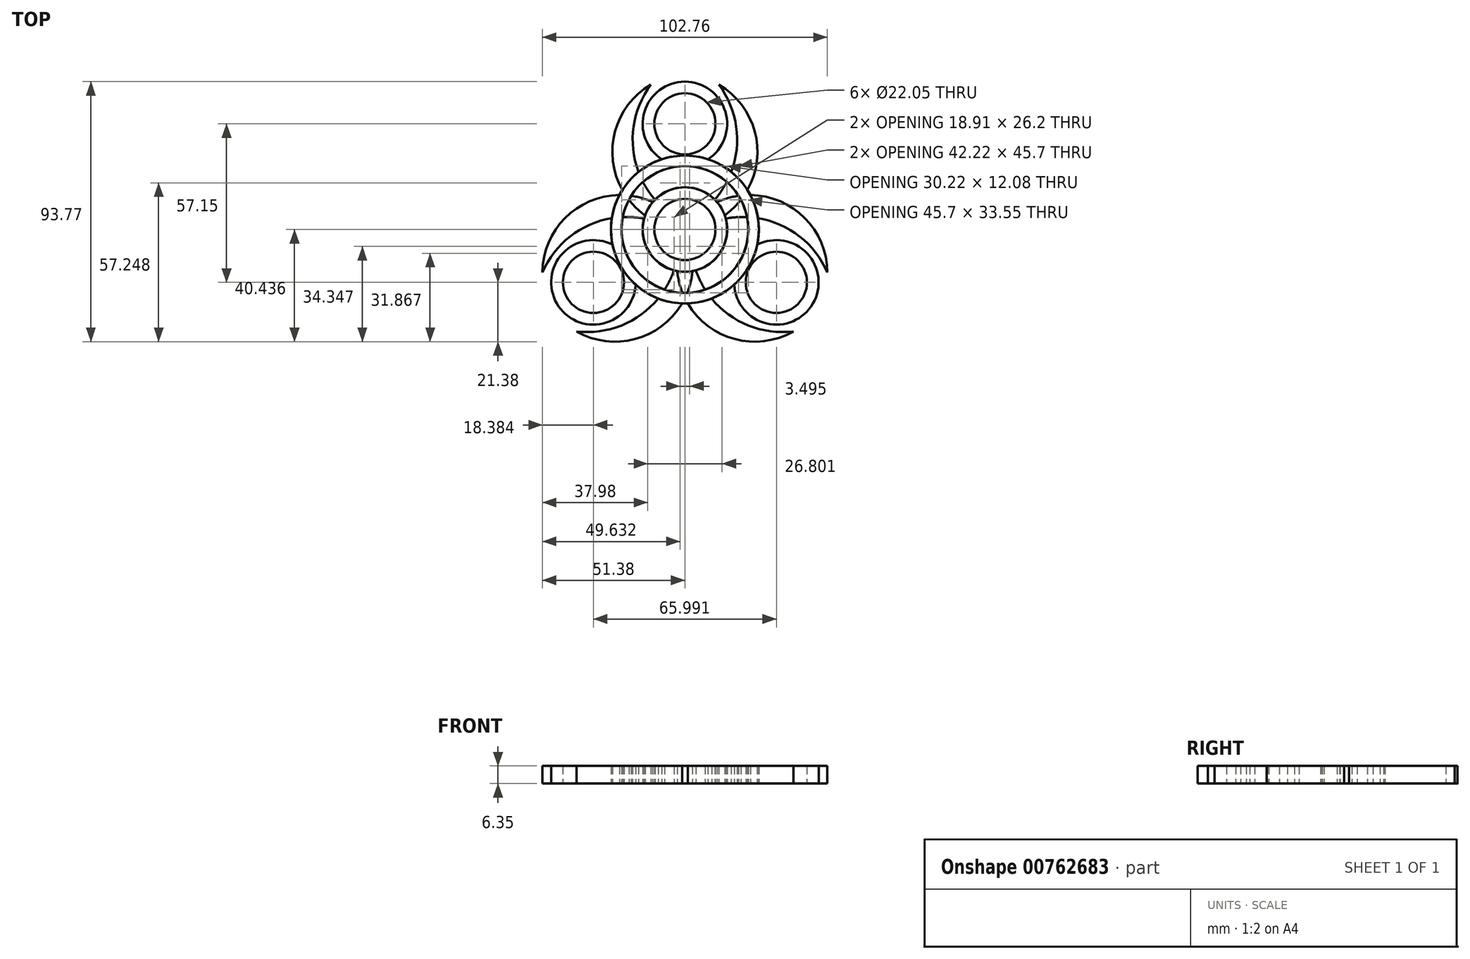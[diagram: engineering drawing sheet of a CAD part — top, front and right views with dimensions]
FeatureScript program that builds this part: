
annotation { "Feature Type Name" : "Feature", "Feature Type Description" : "" }
export const myFeature = defineFeature(function(context is Context, id is Id, definition is map)
    precondition{}
    {
        {
            var Q0;
            Q0=qCreatedBy(makeId("Top.planeOp"),FACE);
            var sketch = newSketch(context, id + "F0", { "sketchPlane" : qUnion([Q0])});
            skCircle(sketch, "E0", {"center": v(0, 0) * mm, "radius": 15.24 * mm});
            skCircle(sketch, "E1", {"center": v(0, 0) * mm, "radius": 11.02 * mm});
            skCircle(sketch, "E2", {"center": v(0, 0) * mm, "radius": 26.67 * mm});
            skCircle(sketch, "E3", {"center": v(0, 0) * mm, "radius": 22.86 * mm});
            skCircle(sketch, "E4", {"center": v(0, 38.1) * mm, "radius": 15.24 * mm});
            skCircle(sketch, "E5", {"center": v(0, 38.1) * mm, "radius": 11.02 * mm});
            skArc(sketch, "E6", {"start": v(-12.25, 52.25) * mm, "mid": v(-18.83, 31.26) * mm, "end": v(-10.78, 10.78) * mm});
            skArc(sketch, "E7", {"start": v(-12.25, 52.25) * mm, "mid": v(-26.15, 29.26) * mm, "end": v(-14.36, 5.12) * mm});
            skArc(sketch, "E8.MirrorCS", {"start": v(12.25, 52.25) * mm, "mid": v(18.83, 31.26) * mm, "end": v(10.78, 10.78) * mm});
            skArc(sketch, "E9.MirrorCS", {"start": v(12.25, 52.25) * mm, "mid": v(26.15, 29.26) * mm, "end": v(14.36, 5.12) * mm});
            skSolve(sketch);
        }
        {
            var Q0;
            {var subQ0=sQuery(id+"F0.wireOp",EDGE,"E6");var subQ1=sQuery(id+"F0.wireOp",EDGE,"E2");var subQ2=makeQuery(id+"F0.imprint","INTERSECT",VERTEX,{"derivedFrom":[subQ1,subQ0]});Q0=makeQuery(id+"F0.imprint","IMPRINT",FACE,{"disambiguationData":[TD([[makeQuery(id+"F0.imprint","IMPRINT",EDGE,{"disambiguationData":[TD([[subQ2,-1.0]])],"derivedFrom":subQ1}),-1.0]])]});}
            var Q1;
            Q1=makeQuery(id+"F0.imprint","IMPRINT",FACE,{"disambiguationData":[TD([[makeQuery(id+"F0.imprint","IMPRINT",EDGE,{"derivedFrom":sQuery(id+"F0.wireOp",EDGE,"E5")}),-1.0]])]});
            var Q2;
            {var subQ0=sQuery(id+"F0.wireOp",EDGE,"E4");var subQ1=sQuery(id+"F0.wireOp",EDGE,"E2");var subQ2=makeQuery(id+"F0.imprint","INTERSECT",VERTEX,{"disambiguationData":[OD(0.0)],"derivedFrom":[subQ1,subQ0]});Q2=makeQuery(id+"F0.imprint","IMPRINT",FACE,{"disambiguationData":[TD([[makeQuery(id+"F0.imprint","IMPRINT",EDGE,{"disambiguationData":[TD([[subQ2,-1.0]])],"derivedFrom":subQ1}),1.0]])]});}
            var Q3;
            {var subQ0=sQuery(id+"F0.wireOp",EDGE,"E4");var subQ1=sQuery(id+"F0.wireOp",EDGE,"E2");var subQ2=makeQuery(id+"F0.imprint","INTERSECT",VERTEX,{"disambiguationData":[OD(1.0)],"derivedFrom":[subQ1,subQ0]});Q3=makeQuery(id+"F0.imprint","IMPRINT",FACE,{"disambiguationData":[TD([[makeQuery(id+"F0.imprint","IMPRINT",EDGE,{"disambiguationData":[TD([[subQ2,-1.0]])],"derivedFrom":subQ1}),1.0]])]});}
            var Q4;
            {var subQ0=sQuery(id+"F0.wireOp",EDGE,"E6");var subQ1=sQuery(id+"F0.wireOp",EDGE,"E2");var subQ2=makeQuery(id+"F0.imprint","INTERSECT",VERTEX,{"derivedFrom":[subQ1,subQ0]});Q4=makeQuery(id+"F0.imprint","IMPRINT",FACE,{"disambiguationData":[TD([[makeQuery(id+"F0.imprint","IMPRINT",EDGE,{"disambiguationData":[TD([[subQ2,-1.0]])],"derivedFrom":subQ1}),1.0]])]});}
            var Q5;
            {var subQ0=sQuery(id+"F0.wireOp",EDGE,"E6");var subQ1=sQuery(id+"F0.wireOp",EDGE,"E0");var subQ2=makeQuery(id+"F0.imprint","INTERSECT",VERTEX,{"derivedFrom":[subQ1,subQ0]});Q5=makeQuery(id+"F0.imprint","IMPRINT",FACE,{"disambiguationData":[TD([[makeQuery(id+"F0.imprint","IMPRINT",EDGE,{"disambiguationData":[TD([[subQ2,-1.0]])],"derivedFrom":subQ1}),-1.0]])]});}
            var Q6;
            {var subQ0=sQuery(id+"F0.wireOp",EDGE,"E9.MirrorCS");var subQ1=sQuery(id+"F0.wireOp",EDGE,"E2");var subQ2=makeQuery(id+"F0.imprint","INTERSECT",VERTEX,{"derivedFrom":[subQ1,subQ0]});Q6=makeQuery(id+"F0.imprint","IMPRINT",FACE,{"disambiguationData":[TD([[makeQuery(id+"F0.imprint","IMPRINT",EDGE,{"disambiguationData":[TD([[subQ2,1.0]])],"derivedFrom":subQ1}),1.0]])]});}
            var Q7;
            Q7=makeQuery(id+"F0.imprint","IMPRINT",FACE,{"disambiguationData":[TD([[makeQuery(id+"F0.imprint","IMPRINT",EDGE,{"derivedFrom":sQuery(id+"F0.wireOp",EDGE,"E1")}),-1.0]])]});
            var Q8;
            {var subQ0=sQuery(id+"F0.wireOp",EDGE,"E8.MirrorCS");var subQ1=sQuery(id+"F0.wireOp",EDGE,"E2");var subQ2=makeQuery(id+"F0.imprint","INTERSECT",VERTEX,{"derivedFrom":[subQ1,subQ0]});Q8=makeQuery(id+"F0.imprint","IMPRINT",FACE,{"disambiguationData":[TD([[makeQuery(id+"F0.imprint","IMPRINT",EDGE,{"disambiguationData":[TD([[subQ2,1.0]])],"derivedFrom":subQ1}),1.0]])]});}
            var Q9;
            {var subQ0=sQuery(id+"F0.wireOp",EDGE,"E8.MirrorCS");var subQ1=sQuery(id+"F0.wireOp",EDGE,"E2");var subQ2=makeQuery(id+"F0.imprint","INTERSECT",VERTEX,{"derivedFrom":[subQ1,subQ0]});Q9=makeQuery(id+"F0.imprint","IMPRINT",FACE,{"disambiguationData":[TD([[makeQuery(id+"F0.imprint","IMPRINT",EDGE,{"disambiguationData":[TD([[subQ2,1.0]])],"derivedFrom":subQ1}),-1.0]])]});}
            var Q10;
            {var subQ0=sQuery(id+"F0.wireOp",EDGE,"E8.MirrorCS");var subQ1=sQuery(id+"F0.wireOp",EDGE,"E2");var subQ2=makeQuery(id+"F0.imprint","INTERSECT",VERTEX,{"derivedFrom":[subQ1,subQ0]});Q10=makeQuery(id+"F0.imprint","IMPRINT",FACE,{"disambiguationData":[TD([[makeQuery(id+"F0.imprint","IMPRINT",EDGE,{"disambiguationData":[TD([[subQ2,-1.0]])],"derivedFrom":subQ1}),1.0]])]});}
            var Q11;
            {var subQ0=sQuery(id+"F0.wireOp",EDGE,"E8.MirrorCS");var subQ1=sQuery(id+"F0.wireOp",EDGE,"E0");var subQ2=makeQuery(id+"F0.imprint","INTERSECT",VERTEX,{"derivedFrom":[subQ1,subQ0]});Q11=makeQuery(id+"F0.imprint","IMPRINT",FACE,{"disambiguationData":[TD([[makeQuery(id+"F0.imprint","IMPRINT",EDGE,{"disambiguationData":[TD([[subQ2,1.0]])],"derivedFrom":subQ1}),-1.0]])]});}
            extrude(context, id + "F1", {"entities" : qUnion([Q0, Q1, Q2, Q3, Q4, Q5, Q6, Q7, Q8, Q9, Q10, Q11]), "depth" : 6.35 * mm, "offsetDistance" : 25.4 * mm});
        }
        {
            var Q0;
            Q0=makeQuery(id+"F1.opExtrude","SWEPT_BODY",BODY,{"disambiguationData":[OSD([sQuery(id+"F0.wireOp",EDGE,"E0"),sQuery(id+"F0.wireOp",EDGE,"E1"),sQuery(id+"F0.wireOp",EDGE,"E2"),sQuery(id+"F0.wireOp",EDGE,"E3"),sQuery(id+"F0.wireOp",EDGE,"E4"),sQuery(id+"F0.wireOp",EDGE,"E5"),sQuery(id+"F0.wireOp",EDGE,"E6"),sQuery(id+"F0.wireOp",EDGE,"E7"),sQuery(id+"F0.wireOp",EDGE,"E8.MirrorCS"),sQuery(id+"F0.wireOp",EDGE,"E9.MirrorCS")])]});
            var Q1;
            Q1=makeQuery(id+"F1.opExtrude","CAP_EDGE",EDGE,{"disambiguationData":[OSD([sQuery(id+"F0.wireOp",EDGE,"E1")])],"isStart":false});
            circularPattern(context, id + "F2", {"entities" : qUnion([Q0]), "axis" : qUnion([Q1]), "angle" : 360 * degree, "instanceCount" : 3, "equalSpace" : true});
        }
    });
